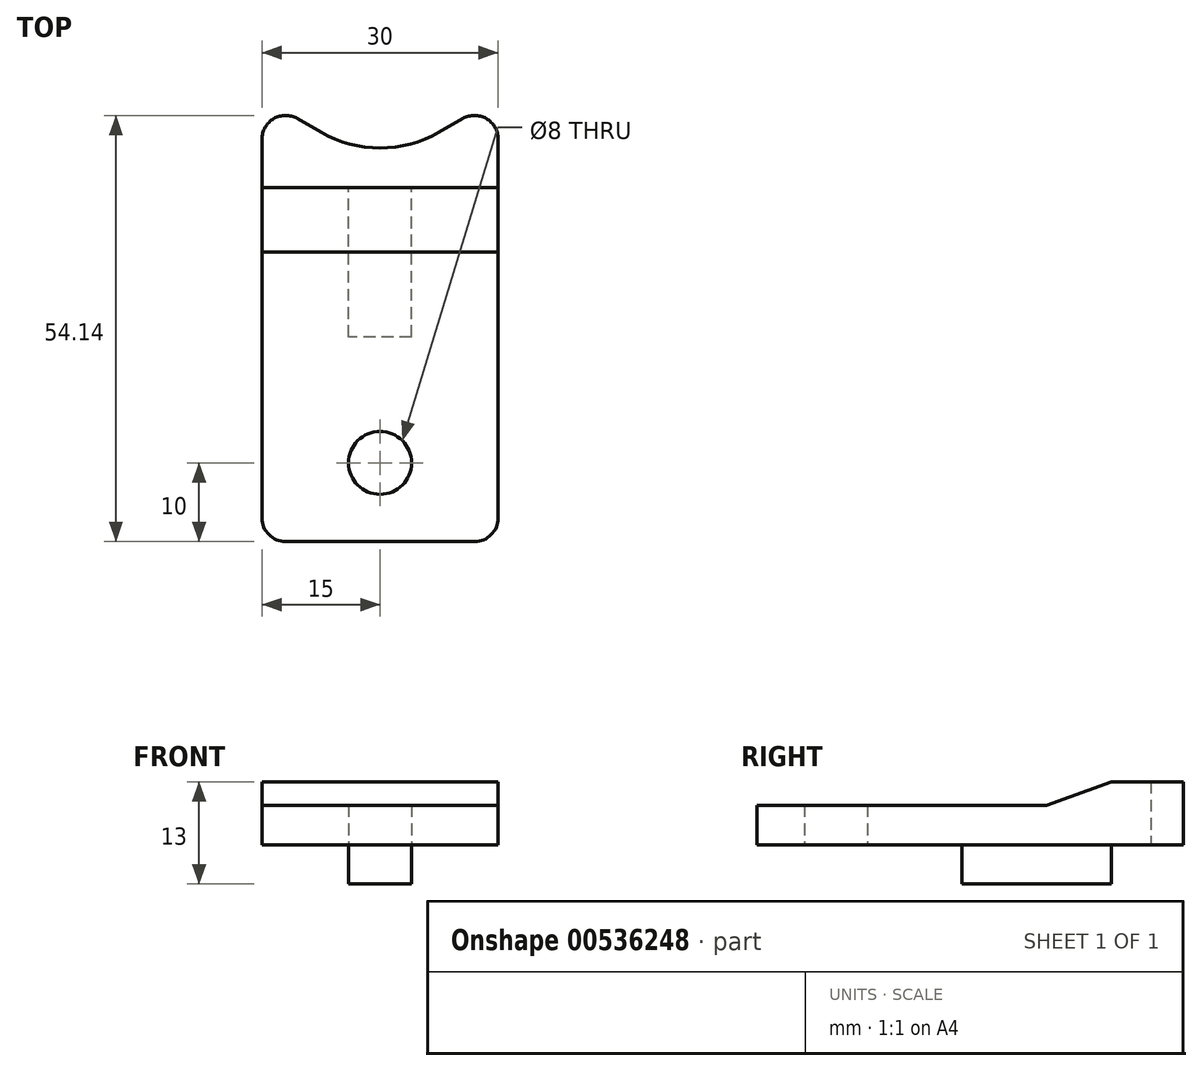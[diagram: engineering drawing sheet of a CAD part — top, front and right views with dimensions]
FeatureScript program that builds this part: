
annotation { "Feature Type Name" : "Feature", "Feature Type Description" : "" }
export const myFeature = defineFeature(function(context is Context, id is Id, definition is map)
    precondition{}
    {
        {
            var Q0;
            Q0=qCreatedBy(makeId("Top.planeOp"),FACE);
            var sketch = newSketch(context, id + "F0", { "sketchPlane" : qUnion([Q0])});
            skLineSegment(sketch, "E0.top", {"start": v(-15, -25) * mm, "end": v(15, -25) * mm});
            skLineSegment(sketch, "E0.left", {"start": v(-15, 25) * mm, "end": v(-15, -25) * mm});
            skLineSegment(sketch, "E0.right", {"start": v(15, 25) * mm, "end": v(15, -25) * mm});
            skPoint(sketch, "E0.middle", {"position": v(0, 0) * mm});
            skCircle(sketch, "E1", {"center": v(0, -15) * mm, "radius": 4 * mm});
            skArc(sketch, "E2", {"start": v(-7.5, 27) * mm, "mid": v(0, 25) * mm, "end": v(7.5, 27) * mm});
            skLineSegment(sketch, "E3", {"start": v(7.5, 27) * mm, "end": v(15, 31.34) * mm});
            skLineSegment(sketch, "E4", {"start": v(15, 25) * mm, "end": v(15, 31.34) * mm});
            skLineSegment(sketch, "E5.MirrorCS", {"start": v(-7.5, 27) * mm, "end": v(-15, 31.34) * mm});
            skLineSegment(sketch, "E6.MirrorCS", {"start": v(-15, 25) * mm, "end": v(-15, 31.34) * mm});
            skLineSegment(sketch, "E7.bottom", {"start": v(4, 1) * mm, "end": v(-4, 1) * mm});
            skLineSegment(sketch, "E7.top", {"start": v(4, 21) * mm, "end": v(-4, 21) * mm});
            skLineSegment(sketch, "E7.left", {"start": v(4, 1) * mm, "end": v(4, 21) * mm});
            skLineSegment(sketch, "E7.right", {"start": v(-4, 1) * mm, "end": v(-4, 21) * mm});
            skPoint(sketch, "E7.middle", {"position": v(0, 11) * mm});
            skLineSegment(sketch, "E8", {"start": v(-15, 20) * mm, "end": v(15, 20) * mm});
            skSolve(sketch);
        }
        {
            var Q0;
            Q0=makeQuery(id+"F0.imprint","IMPRINT",FACE,{"disambiguationData":[TD([[makeQuery(id+"F0.imprint","IMPRINT",EDGE,{"derivedFrom":sQuery(id+"F0.wireOp",EDGE,"E0.top")}),1.0]])]});
            var Q1;
            Q1=makeQuery(id+"F0.imprint","IMPRINT",FACE,{"disambiguationData":[TD([[makeQuery(id+"F0.imprint","IMPRINT",EDGE,{"derivedFrom":sQuery(id+"F0.wireOp",EDGE,"E7.bottom")}),-1.0]])]});
            var Q2;
            Q2=makeQuery(id+"F0.imprint","IMPRINT",FACE,{"disambiguationData":[TD([[makeQuery(id+"F0.imprint","IMPRINT",EDGE,{"derivedFrom":sQuery(id+"F0.wireOp",EDGE,"E2")}),-1.0]])]});
            extrude(context, id + "F1", {"entities" : qUnion([Q0, Q1, Q2]), "depth" : 5 * mm, "offsetDistance" : 25 * mm});
        }
        {
            var Q0;
            {var subQ0=sQuery(id+"F0.wireOp",EDGE,"E7.top");Q0=makeQuery(id+"F0.imprint","IMPRINT",FACE,{"disambiguationData":[TD([[makeQuery(id+"F0.imprint","IMPRINT",EDGE,{"derivedFrom":subQ0}),1.0]])]});}
            var Q1;
            Q1=makeQuery(id+"F0.imprint","IMPRINT",FACE,{"disambiguationData":[TD([[makeQuery(id+"F0.imprint","IMPRINT",EDGE,{"derivedFrom":sQuery(id+"F0.wireOp",EDGE,"E2")}),-1.0]])]});
            extrude(context, id + "F2", {"entities" : qUnion([Q0, Q1]), "operationType" : NewBodyOperationType.ADD, "depth" : 8 * mm, "offsetDistance" : 25 * mm});
        }
        {
            var Q0;
            Q0=makeQuery(id+"F0.imprint","IMPRINT",FACE,{"disambiguationData":[TD([[makeQuery(id+"F0.imprint","IMPRINT",EDGE,{"derivedFrom":sQuery(id+"F0.wireOp",EDGE,"E7.bottom")}),-1.0]])]});
            extrude(context, id + "F3", {"entities" : qUnion([Q0]), "operationType" : NewBodyOperationType.ADD, "oppositeDirection" : true, "depth" : 5 * mm, "offsetDistance" : 25 * mm});
        }
        {
            var Q0;
            {var subQ0=sQuery(id+"F0.wireOp",EDGE,"E6.MirrorCS");var subQ1=sQuery(id+"F0.wireOp",EDGE,"E5.MirrorCS");Q0=makeQuery(id+"F2.boolean.opBoolean","MERGE",EDGE,{"derivedFrom":[makeQuery(id+"F1.opExtrude","SWEPT_EDGE",EDGE,{"disambiguationData":[OSD([subQ1,subQ0])]}),makeQuery(id+"F2.opExtrude","SWEPT_EDGE",EDGE,{"disambiguationData":[OSD([subQ1,subQ0])]})]});}
            var Q1;
            {var subQ0=sQuery(id+"F0.wireOp",EDGE,"E4");var subQ1=sQuery(id+"F0.wireOp",EDGE,"E3");Q1=makeQuery(id+"F2.boolean.opBoolean","MERGE",EDGE,{"derivedFrom":[makeQuery(id+"F1.opExtrude","SWEPT_EDGE",EDGE,{"disambiguationData":[OSD([subQ1,subQ0])]}),makeQuery(id+"F2.opExtrude","SWEPT_EDGE",EDGE,{"disambiguationData":[OSD([subQ1,subQ0])]})]});}
            var Q2;
            Q2=makeQuery(id+"F1.opExtrude","SWEPT_EDGE",EDGE,{"disambiguationData":[OSD([sQuery(id+"F0.wireOp",EDGE,"E0.top"),sQuery(id+"F0.wireOp",EDGE,"E0.left")])]});
            var Q3;
            Q3=makeQuery(id+"F1.opExtrude","SWEPT_EDGE",EDGE,{"disambiguationData":[OSD([sQuery(id+"F0.wireOp",EDGE,"E0.top"),sQuery(id+"F0.wireOp",EDGE,"E0.right")])]});
            fillet(context, id + "F4", {"entities" : qUnion([Q0, Q1, Q2, Q3]), "radius" : 3 * mm, "tangentPropagation" : true, "allowEdgeOverflow" : false});
        }
        {
            var Q0;
            {var subQ0=sQuery(id+"F0.wireOp",EDGE,"E8");Q0=makeQuery(id+"F2.boolean.opBoolean","INTERSECT",EDGE,{"derivedFrom":[makeQuery(id+"F1.opExtrude","CAP_FACE",FACE,{"disambiguationData":[OSD([sQuery(id+"F0.wireOp",EDGE,"E0.top"),sQuery(id+"F0.wireOp",EDGE,"E0.left"),sQuery(id+"F0.wireOp",EDGE,"E0.right"),sQuery(id+"F0.wireOp",EDGE,"E1"),sQuery(id+"F0.wireOp",EDGE,"E2"),sQuery(id+"F0.wireOp",EDGE,"E3"),sQuery(id+"F0.wireOp",EDGE,"E4"),sQuery(id+"F0.wireOp",EDGE,"E5.MirrorCS"),sQuery(id+"F0.wireOp",EDGE,"E6.MirrorCS"),sQuery(id+"F0.wireOp",EDGE,"E7.top"),sQuery(id+"F0.wireOp",EDGE,"E7.left"),sQuery(id+"F0.wireOp",EDGE,"E7.right"),subQ0])],"isStart":false}),makeQuery(id+"F2.opExtrude","SWEPT_FACE",FACE,{"disambiguationData":[OSD([subQ0])]})]});}
            chamfer(context, id + "F5", {"entities" : qUnion([Q0]), "chamferType" : ChamferType.OFFSET_ANGLE, "width" : 3 * mm, "oppositeDirection" : false, "angle" : 70 * degree, "tangentPropagation" : true});
        }
    });
